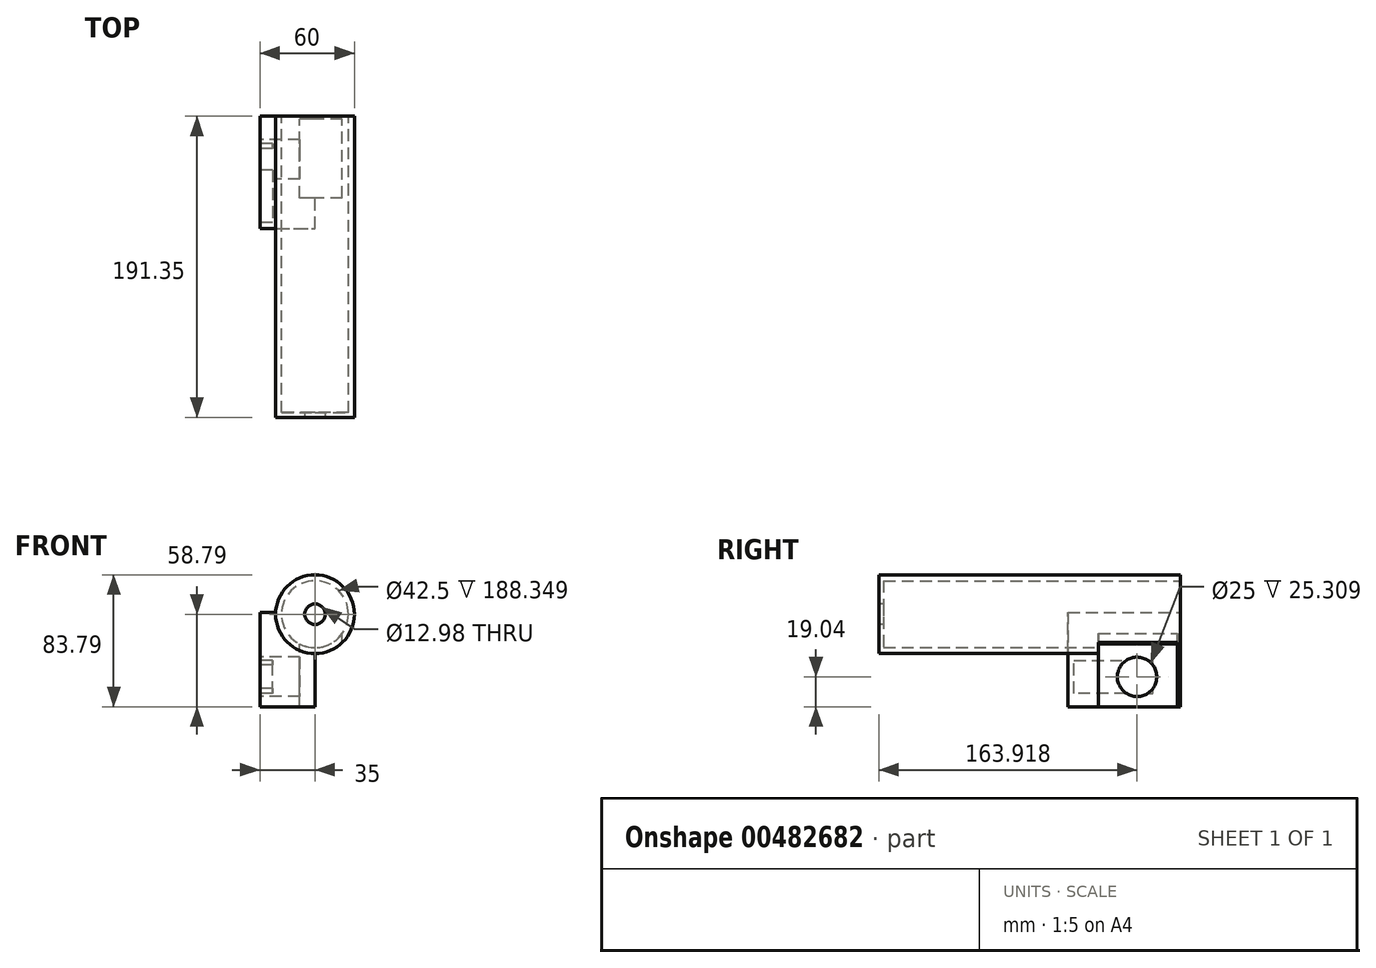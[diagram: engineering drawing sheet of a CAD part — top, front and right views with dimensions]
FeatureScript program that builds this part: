
annotation { "Feature Type Name" : "Feature", "Feature Type Description" : "" }
export const myFeature = defineFeature(function(context is Context, id is Id, definition is map)
    precondition{}
    {
        {
            var Q0;
            Q0=qCreatedBy(makeId("Front.planeOp"),FACE);
            var sketch = newSketch(context, id + "F0", { "sketchPlane" : qUnion([Q0])});
            skCircle(sketch, "E0", {"center": v(0, 0) * mm, "radius": 25 * mm});
            skSolve(sketch);
        }
        {
            var Q0;
            Q0 = qSketchRegion(id + "F0", true);
            extrude(context, id + "F1", {"entities" : qUnion([Q0]), "depth" : 200 * mm});
        }
        {
            var Q0;
            Q0=makeQuery(id+"F1.opExtrude","CAP_FACE",FACE,{"disambiguationData":[OSD([sQuery(id+"F0.wireOp",EDGE,"E0")])],"isStart":true});
            var sketch = newSketch(context, id + "F2", { "sketchPlane" : qUnion([Q0])});
            skCircle(sketch, "E1", {"center": v(0, 0) * mm, "radius": 21.25 * mm});
            skSolve(sketch);
        }
        {
            var Q0;
            Q0=qCreatedBy(makeId("Top.planeOp"),FACE);
            var sketch = newSketch(context, id + "F3", { "sketchPlane" : qUnion([Q0])});
            skLineSegment(sketch, "E2.bottom", {"start": v(17.3, -60.57) * mm, "end": v(-9.7, -60.57) * mm});
            skLineSegment(sketch, "E2.top", {"start": v(17.3, -10.57) * mm, "end": v(-9.7, -10.57) * mm});
            skLineSegment(sketch, "E2.left", {"start": v(17.3, -60.57) * mm, "end": v(17.3, -10.57) * mm});
            skLineSegment(sketch, "E2.right", {"start": v(-9.7, -60.57) * mm, "end": v(-9.7, -10.57) * mm});
            skSolve(sketch);
        }
        {
            var Q0;
            Q0=qCreatedBy(makeId("Front.planeOp"),FACE);
            var sketch = newSketch(context, id + "F4", { "sketchPlane" : qUnion([Q0])});
            skLineSegment(sketch, "E3.bottom", {"start": v(-35, -58.8) * mm, "end": v(0, -58.8) * mm});
            skLineSegment(sketch, "E3.top", {"start": v(-35, 1.2) * mm, "end": v(0, 1.2) * mm});
            skLineSegment(sketch, "E3.left", {"start": v(-35, -58.8) * mm, "end": v(-35, 1.2) * mm});
            skLineSegment(sketch, "E3.right", {"start": v(0, -58.8) * mm, "end": v(0, 1.2) * mm});
            skSolve(sketch);
        }
        {
            var Q0;
            Q0 = qSketchRegion(id + "F4", true);
            extrude(context, id + "F5", {"entities" : qUnion([Q0]), "operationType" : NewBodyOperationType.ADD, "depth" : 80 * mm});
        }
        {
            var Q0;
            Q0=makeQuery(id+"F2.imprint","IMPRINT",FACE,{"disambiguationData":[TD([[makeQuery(id+"F2.imprint","IMPRINT",EDGE,{"derivedFrom":sQuery(id+"F2.wireOp",EDGE,"E1")}),1.0]])]});
            extrude(context, id + "F6", {"entities" : qUnion([Q0]), "operationType" : NewBodyOperationType.REMOVE, "oppositeDirection" : true, "depth" : 197 * mm});
        }
        {
            var Q0;
            Q0=makeQuery(id+"F5.opExtrude","SWEPT_FACE",FACE,{"disambiguationData":[OSD([sQuery(id+"F4.wireOp",EDGE,"E3.left")])]});
            var sketch = newSketch(context, id + "F7", { "sketchPlane" : qUnion([Q0])});
            skCircle(sketch, "E4", {"center": v(36.08, -39.75) * mm, "radius": 11.75 * mm});
            skLineSegment(sketch, "E5", {"start": v(36.08, -29.25) * mm, "end": v(36.08, -50.25) * mm});
            skLineSegment(sketch, "E6", {"start": v(36.08, -50.25) * mm, "end": v(26.08, -50.25) * mm});
            skLineSegment(sketch, "E7", {"start": v(36.08, -50.25) * mm, "end": v(76.08, -50.25) * mm});
            skLineSegment(sketch, "E8", {"start": v(76.08, -50.25) * mm, "end": v(76.08, -29.25) * mm});
            skLineSegment(sketch, "E9", {"start": v(76.08, -29.25) * mm, "end": v(26.08, -29.25) * mm});
            skLineSegment(sketch, "E10", {"start": v(26.08, -50.25) * mm, "end": v(26.08, -29.25) * mm});
            skLineSegment(sketch, "E11", {"start": v(36.08, -39.75) * mm, "end": v(55.08, -39.75) * mm, "construction": true});
            skLineSegment(sketch, "E12", {"start": v(36.08, -39.75) * mm, "end": v(18.72, -39.75) * mm, "construction": true});
            skPoint(sketch, "E12.endSnap0", {"position": v(26.08, -39.75) * mm});
            skLineSegment(sketch, "E13", {"start": v(0, 27.25) * mm, "end": v(57.77, 27.25) * mm});
            skLineSegment(sketch, "E14.0", {"start": v(0, -21.25) * mm, "end": v(0, 21.25) * mm});
            skLineSegment(sketch, "E15", {"start": v(0, 21.25) * mm, "end": v(131.82, 21.25) * mm});
            skLineSegment(sketch, "E16", {"start": v(46.8, 21.25) * mm, "end": v(131.82, 21.25) * mm, "construction": true});
            skLineSegment(sketch, "E17", {"start": v(131.82, 21.25) * mm, "end": v(0, 21.25) * mm, "construction": true});
            skSolve(sketch);
        }
        {
            var Q0;
            Q0 = qSketchRegion(id + "F3", true);
            extrude(context, id + "F8", {"entities" : qUnion([Q0]), "operationType" : NewBodyOperationType.REMOVE, "oppositeDirection" : true, "depth" : 60 * mm});
        }
        {
            var Q0;
            {var subQ5=sQuery(id+"F7.wireOp",EDGE,"E8");Q0=makeQuery(id+"F7.imprint","IMPRINT",FACE,{"disambiguationData":[TD([[makeQuery(id+"F7.imprint","IMPRINT",EDGE,{"derivedFrom":subQ5}),1.0]])]});}
            var Q1;
            {var subQ5=sQuery(id+"F7.wireOp",EDGE,"E10");Q1=makeQuery(id+"F7.imprint","IMPRINT",FACE,{"disambiguationData":[TD([[makeQuery(id+"F7.imprint","IMPRINT",EDGE,{"derivedFrom":subQ5}),-1.0]])]});}
            extrude(context, id + "F9", {"entities" : qUnion([Q0, Q1]), "operationType" : NewBodyOperationType.REMOVE, "oppositeDirection" : true, "depth" : 8 * mm});
        }
        {
            var Q0;
            Q0=makeQuery(id+"F5.opExtrude","SWEPT_FACE",FACE,{"disambiguationData":[OSD([sQuery(id+"F4.wireOp",EDGE,"E3.bottom")])]});
            var sketch = newSketch(context, id + "F10", { "sketchPlane" : qUnion([Q0])});
            skLineSegment(sketch, "E18.bottom", {"start": v(-35, 8.65) * mm, "end": v(47.15, 8.65) * mm});
            skLineSegment(sketch, "E18.top", {"start": v(-35, 0) * mm, "end": v(47.15, 0) * mm});
            skLineSegment(sketch, "E18.left", {"start": v(-35, 8.65) * mm, "end": v(-35, 0) * mm});
            skLineSegment(sketch, "E18.right", {"start": v(47.15, 8.65) * mm, "end": v(47.15, 0) * mm});
            skSolve(sketch);
        }
        {
            var Q0;
            Q0=makeQuery(id+"F5.opExtrude","SWEPT_FACE",FACE,{"disambiguationData":[OSD([sQuery(id+"F4.wireOp",EDGE,"E3.bottom")])]});
            var sketch = newSketch(context, id + "F11", { "sketchPlane" : qUnion([Q0])});
            skSolve(sketch);
        }
        {
            var Q0;
            {var subQ0=sQuery(id+"F10.wireOp",EDGE,"E18.right");Q0=makeQuery(id+"F10.imprint","IMPRINT",FACE,{"disambiguationData":[TD([[makeQuery(id+"F10.imprint","IMPRINT",EDGE,{"derivedFrom":subQ0}),-1.0]])]});}
            var Q1;
            {var subQ0=sQuery(id+"F10.wireOp",EDGE,"E18.left");Q1=makeQuery(id+"F10.imprint","IMPRINT",FACE,{"disambiguationData":[TD([[makeQuery(id+"F10.imprint","IMPRINT",EDGE,{"derivedFrom":subQ0}),1.0]])]});}
            extrude(context, id + "F12", {"entities" : qUnion([Q0, Q1]), "operationType" : NewBodyOperationType.REMOVE, "endBound" : BoundingType.THROUGH_ALL, "oppositeDirection" : true, "depth" : 25 * mm});
        }
        {
            var Q0;
            Q0=makeQuery(id+"F5.opExtrude","SWEPT_FACE",FACE,{"disambiguationData":[OSD([sQuery(id+"F4.wireOp",EDGE,"E3.left")])]});
            var sketch = newSketch(context, id + "F13", { "sketchPlane" : qUnion([Q0])});
            skCircle(sketch, "E19", {"center": v(36.08, -39.75) * mm, "radius": 12.5 * mm});
            skLineSegment(sketch, "E20.0", {"start": v(36.08, -39.75) * mm, "end": v(18.72, -39.75) * mm});
            skLineSegment(sketch, "E21.0", {"start": v(8.65, 21.25) * mm, "end": v(8.65, -21.25) * mm});
            skLineSegment(sketch, "E22", {"start": v(8.65, 25) * mm, "end": v(200, 25) * mm});
            skLineSegment(sketch, "E23", {"start": v(8.65, 21.25) * mm, "end": v(199.7, 21.25) * mm});
            skSolve(sketch);
        }
        {
            var Q0;
            Q0 = qSketchRegion(id + "F13", true);
            extrude(context, id + "F14", {"entities" : qUnion([Q0]), "operationType" : NewBodyOperationType.REMOVE, "oppositeDirection" : true, "depth" : 50 * mm});
        }
        {
            var Q0;
            Q0=makeQuery(id+"F1.opExtrude","CAP_FACE",FACE,{"disambiguationData":[OSD([sQuery(id+"F0.wireOp",EDGE,"E0")])],"isStart":false});
            var sketch = newSketch(context, id + "F15", { "sketchPlane" : qUnion([Q0])});
            skCircle(sketch, "E24", {"center": v(0, 0) * mm, "radius": 6.49 * mm});
            skSolve(sketch);
        }
        {
            var Q0;
            Q0 = qSketchRegion(id + "F15", true);
            extrude(context, id + "F16", {"entities" : qUnion([Q0]), "operationType" : NewBodyOperationType.REMOVE, "oppositeDirection" : true, "depth" : 25 * mm});
        }
    });
